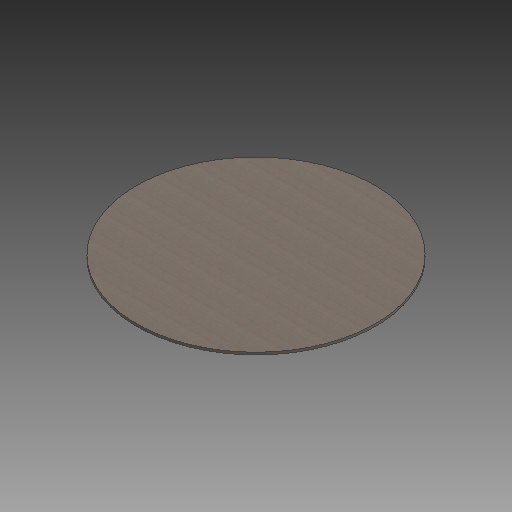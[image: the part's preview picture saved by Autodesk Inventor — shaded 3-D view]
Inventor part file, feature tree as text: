
AUTODESK INVENTOR PART (.ipt)
format: ipt  version: 2020 (Build 240168000, 168)  size: 349,184 bytes
history: native  units: mm
features: other x5, sketch x5, extrude x3, projected_geometry x2, fillet x1
ambient origin geometry x8: Origin, YZ Plane, XZ Plane, XY Plane, X Axis, Y Axis, Z Axis, Center Point
bodies: Body1 (feature_tree)
feature tree (16):
  other  "contour"
  other  "floor_v2.ipt"
  sketch  "Эскиз1"
  extrude  "Выдавливание1"  Depth=10.0mm
  fillet  "Сопряжение1"  Radius=6.0mm
  sketch  "Эскиз2"
  extrude  "Выдавливание2"  Depth=6.0mm
  sketch  "Эскиз3"
  extrude  "Выдавливание3"  Depth=6.0mm
  other  "Твердое тело1::floor_v2.ipt"
  other  "Элемент создания тегов1"
  projected_geometry  "Спроецированная петля1"
  sketch  "Эскиз10"
  sketch  "Эскиз5"
  projected_geometry  "Спроецированная петля2"
  other  "Твердое тело1"
